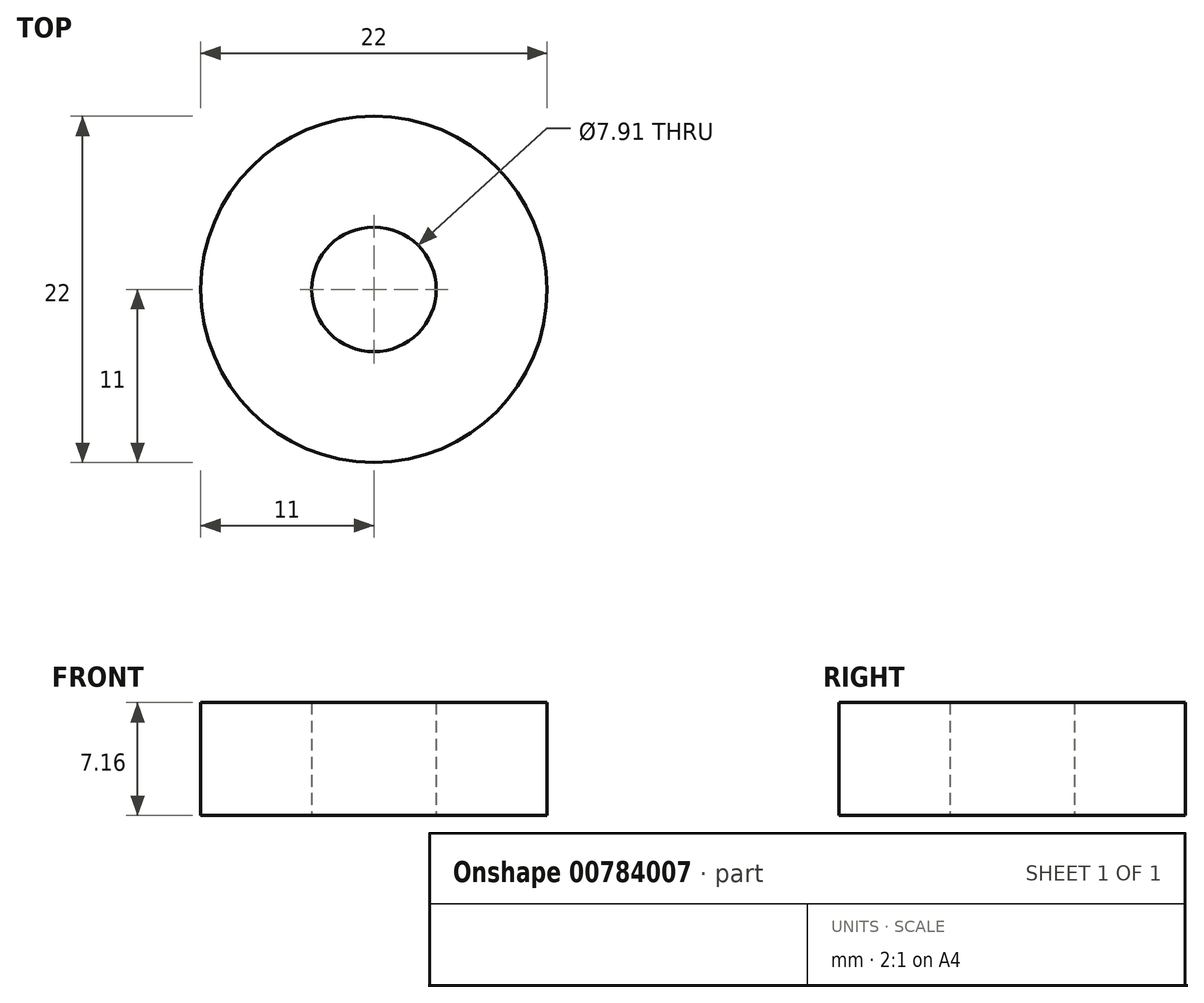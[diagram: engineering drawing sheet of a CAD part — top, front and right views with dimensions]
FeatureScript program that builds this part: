
annotation { "Feature Type Name" : "Feature", "Feature Type Description" : "" }
export const myFeature = defineFeature(function(context is Context, id is Id, definition is map)
    precondition{}
    {
        {
            var Q0;
            Q0=qCreatedBy(makeId("Top.planeOp"),FACE);
            var sketch = newSketch(context, id + "F0", { "sketchPlane" : qUnion([Q0])});
            skCircle(sketch, "E0", {"center": v(0, 0) * mm, "radius": 3.96 * mm});
            skCircle(sketch, "E1", {"center": v(0, 0) * mm, "radius": 11 * mm});
            skSolve(sketch);
        }
        {
            var Q0;
            Q0=makeQuery(id+"F0.imprint","IMPRINT",FACE,{"disambiguationData":[TD([[makeQuery(id+"F0.imprint","IMPRINT",EDGE,{"derivedFrom":sQuery(id+"F0.wireOp",EDGE,"E0")}),-1.0]])]});
            extrude(context, id + "F1", {"entities" : qUnion([Q0]), "depth" : 7.16 * mm, "offsetDistance" : 25.4 * mm});
        }
    });
